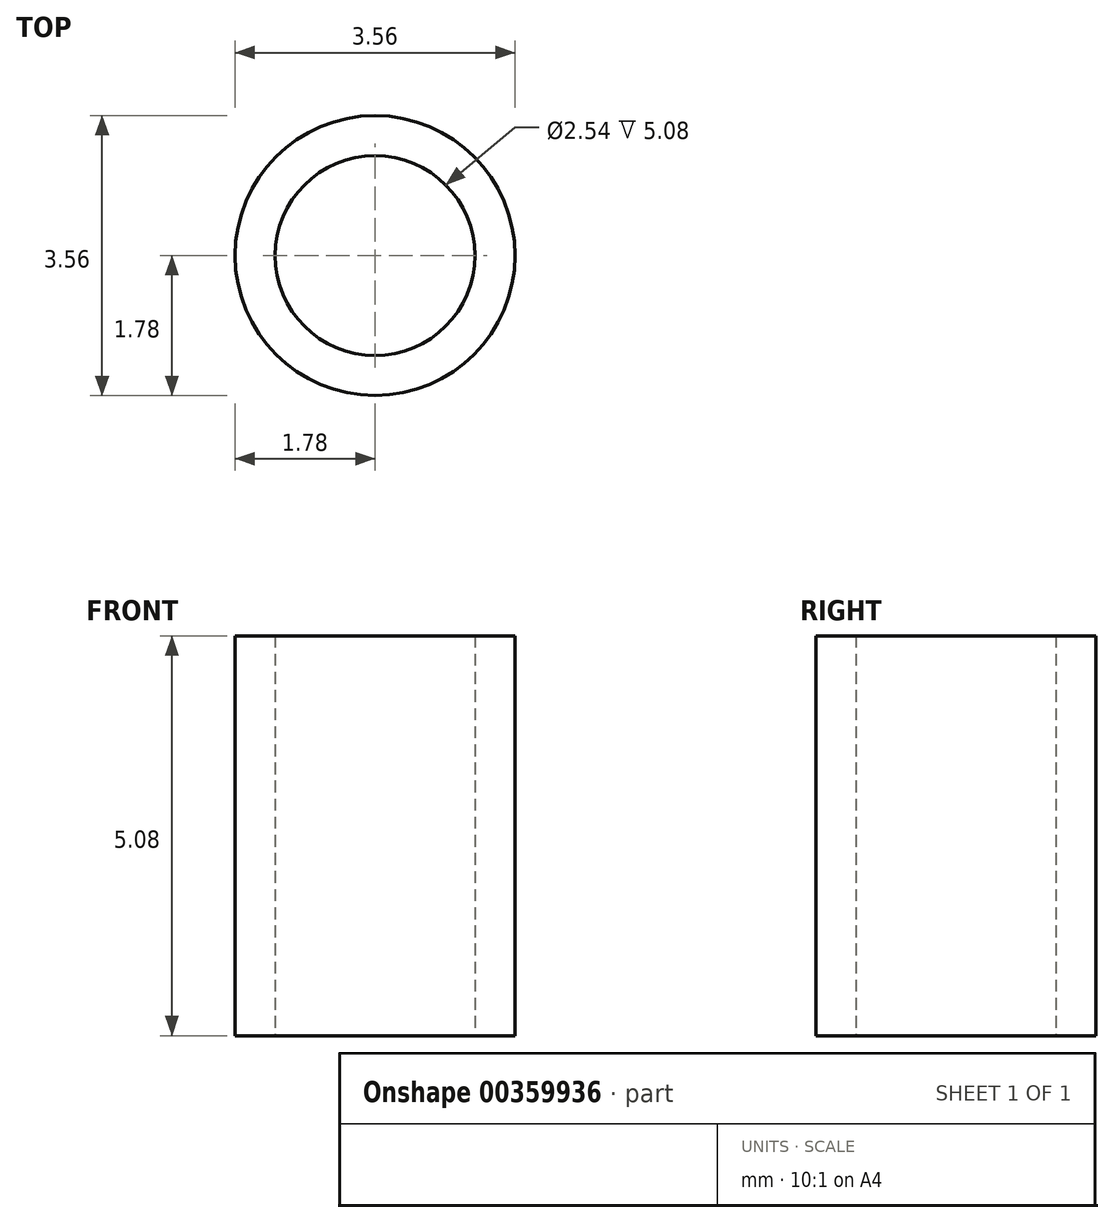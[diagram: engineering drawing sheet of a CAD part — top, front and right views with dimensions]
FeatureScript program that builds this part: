
annotation { "Feature Type Name" : "Feature", "Feature Type Description" : "" }
export const myFeature = defineFeature(function(context is Context, id is Id, definition is map)
    precondition{}
    {
        {
            var Q0;
            Q0=qCreatedBy(makeId("Top.planeOp"),FACE);
            var sketch = newSketch(context, id + "F0", { "sketchPlane" : qUnion([Q0])});
            skPoint(sketch, "E0", {"position": v(1.27, 0) * mm});
            skCircle(sketch, "E1", {"center": v(0, 0) * mm, "radius": 1.27 * mm});
            skPoint(sketch, "E2", {"position": v(1.78, 0) * mm});
            skCircle(sketch, "E3", {"center": v(0, 0) * mm, "radius": 1.78 * mm});
            skSolve(sketch);
        }
        {
            var Q0;
            Q0 = qSketchRegion(id + "F0", true);
            extrude(context, id + "F1", {"entities" : qUnion([Q0]), "depth" : 5.08 * mm});
        }
    });
